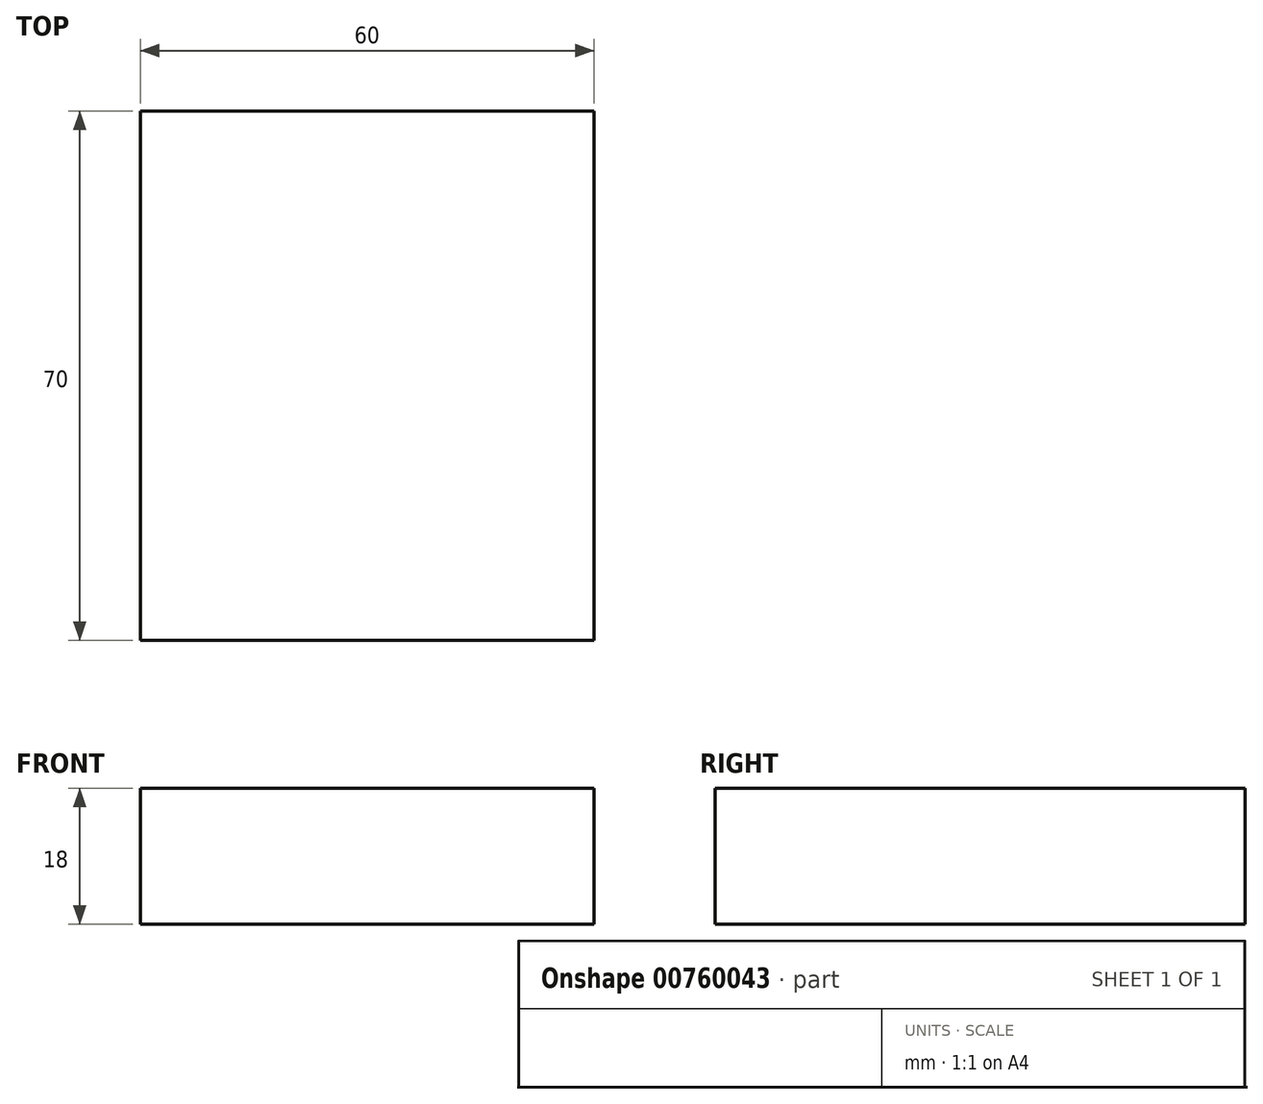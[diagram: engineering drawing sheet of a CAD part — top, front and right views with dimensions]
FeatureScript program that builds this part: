
annotation { "Feature Type Name" : "Feature", "Feature Type Description" : "" }
export const myFeature = defineFeature(function(context is Context, id is Id, definition is map)
    precondition{}
    {
        {
            var Q0;
            Q0=qCreatedBy(makeId("Top.planeOp"),FACE);
            var sketch = newSketch(context, id + "F0", { "sketchPlane" : qUnion([Q0])});
            skLineSegment(sketch, "E0.bottom", {"start": v(30, 35) * mm, "end": v(-30, 35) * mm});
            skLineSegment(sketch, "E0.top", {"start": v(30, -35) * mm, "end": v(-30, -35) * mm});
            skLineSegment(sketch, "E0.left", {"start": v(30, 35) * mm, "end": v(30, -35) * mm});
            skLineSegment(sketch, "E0.right", {"start": v(-30, 35) * mm, "end": v(-30, -35) * mm});
            skSolve(sketch);
        }
        {
            var Q0;
            Q0 = qSketchRegion(id + "F0", true);
            extrude(context, id + "F1", {"entities" : qUnion([Q0]), "depth" : 18 * mm, "offsetDistance" : 25 * mm});
        }
    });
